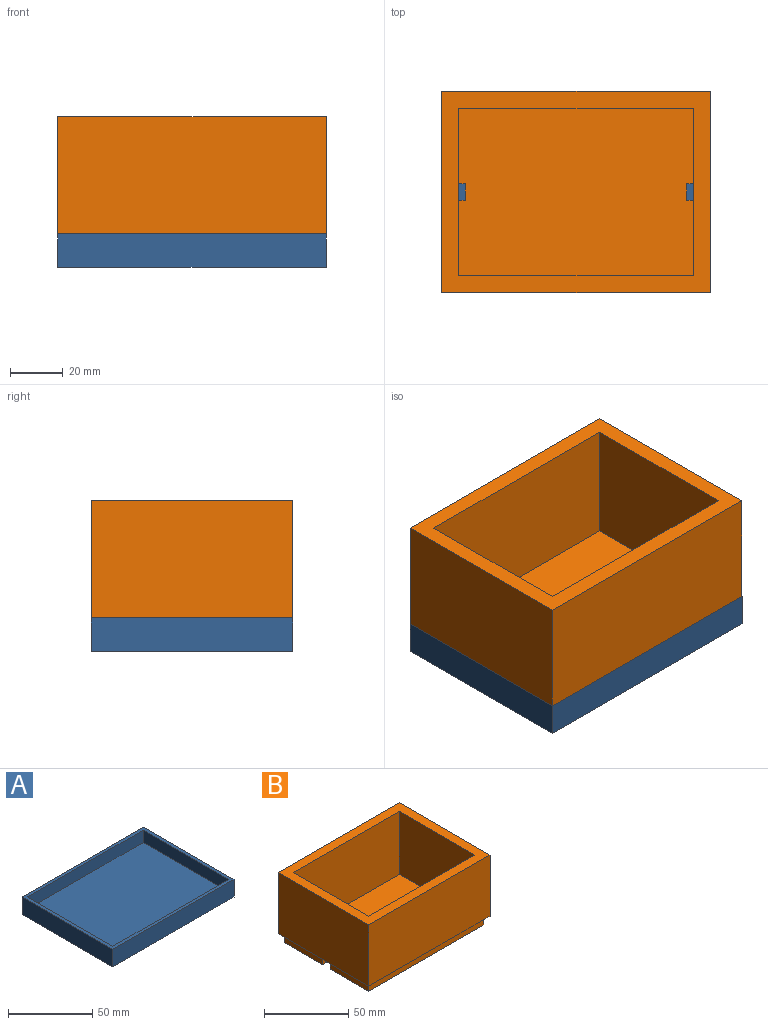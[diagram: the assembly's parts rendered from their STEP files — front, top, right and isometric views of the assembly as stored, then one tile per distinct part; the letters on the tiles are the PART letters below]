
ASSEMBLY  parts=2 mates=1
PART A: 11 faces, bbox 101.6x76.2x12.7 mm
  f0: plane 101.6x76.2mm, normal (0,0,1), area 792mm2, adj f1,f2,f3,f4,f6,f7,f8,f9
  f1: plane 101.6x12.7mm, normal (0,1,0), area 1290.3mm2, adj f0,f2,f4,f5
  f2: plane 76.2x12.7mm, normal (-1,0,0), area 967.7mm2, adj f0,f1,f3,f5
  f3: plane 101.6x12.7mm, normal (0,-1,0), area 1290.3mm2, adj f0,f2,f4,f5
  f4: plane 76.2x12.7mm, normal (1,0,0), area 967.7mm2, adj f0,f1,f3,f5
  f5: plane 101.6x76.2mm, normal (0,0,-1), area 7741.9mm2, adj f1,f2,f3,f4
  f6: plane 97.03x8.89mm, normal (0,-1,0), area 862.6mm2, adj f0,f7,f9,f10
  f7: plane 71.63x8.89mm, normal (1,0,0), area 636.8mm2, adj f0,f6,f8,f10
  f8: plane 97.03x8.89mm, normal (0,1,0), area 862.6mm2, adj f0,f7,f9,f10
  f9: plane 71.63x8.89mm, normal (-1,0,0), area 636.8mm2, adj f0,f6,f8,f10
  f10: plane 97.03x71.63mm, normal (0,0,1), area 6949.9mm2, adj f6,f7,f8,f9
PART B: 24 faces, bbox 101.6x76.2x50.8 mm
  f0: plane 32.39x6.35mm, normal (-1,0,0), area 205.6mm2, adj f14,f16,f17,f21
  f1: plane 88.9x63.5mm, normal (0,0,1), area 5612.9mm2, adj f2,f4,f10,f11,f18,f19,f20,f21
  f2: plane 63.5x45.72mm, normal (1,0,0), area 2895.2mm2, adj f1,f5,f10,f11,f16,f21,f22
  f3: plane 32.39x6.35mm, normal (1,0,0), area 205.6mm2, adj f12,f16,f17,f18
  f4: plane 63.5x45.72mm, normal (-1,0,0), area 2895.2mm2, adj f1,f5,f10,f11,f16,f18,f19
  f5: plane 101.6x76.2mm, normal (0,0,1), area 2096.8mm2, adj f2,f4,f6,f7,f8,f9,f10,f11
  f6: plane 101.6x44.45mm, normal (0,1,0), area 4516.1mm2, adj f5,f7,f9,f16
  f7: plane 76.2x44.45mm, normal (-1,0,0), area 3387.1mm2, adj f5,f6,f8,f16
  f8: plane 101.6x44.45mm, normal (0,-1,0), area 4516.1mm2, adj f5,f7,f9,f16
  f9: plane 76.2x44.45mm, normal (1,0,0), area 3387.1mm2, adj f5,f6,f8,f16
  f10: plane 88.9x45.72mm, normal (0,1,0), area 4064.5mm2, adj f1,f2,f4,f5
  f11: plane 88.9x45.72mm, normal (0,-1,0), area 4064.5mm2, adj f1,f2,f4,f5
  f12: plane 96.52x6.35mm, normal (0,-1,0), area 612.9mm2, adj f3,f15,f16,f17
  f13: plane 32.39x6.35mm, normal (1,0,0), area 205.6mm2, adj f14,f16,f17,f19
  f14: plane 96.52x6.35mm, normal (0,1,0), area 612.9mm2, adj f0,f13,f16,f17
  f15: plane 32.39x6.35mm, normal (-1,0,0), area 205.6mm2, adj f12,f16,f17,f22
  f16: plane 101.6x76.2mm, normal (0,0,-1), area 925.8mm2, adj f0,f2,f3,f4,f6,f7,f8,f9
  f17: plane 96.52x71.12mm, normal (0,0,-1), area 6783.9mm2, adj f0,f3,f12,f13,f14,f15,f18,f19
  f18: plane 6.35x6.35mm, normal (0,1,0), area 37.1mm2, adj f1,f3,f4,f16,f17,f20
  f19: plane 6.35x6.35mm, normal (0,-1,0), area 37.1mm2, adj f1,f4,f13,f16,f17,f20
  f20: plane 6.35x5.08mm, normal (1,0,0), area 32.3mm2, adj f1,f17,f18,f19
  f21: plane 6.35x6.35mm, normal (0,-1,0), area 37.1mm2, adj f0,f1,f2,f16,f17,f23
  f22: plane 6.35x6.35mm, normal (0,1,0), area 37.1mm2, adj f1,f2,f15,f16,f17,f23
  f23: plane 6.35x5.08mm, normal (-1,0,0), area 32.3mm2, adj f1,f17,f21,f22
PLACE A t=(7.22,0.85,-42.6)mm
PLACE B t=(-10.83,12.76,-36.25)mm
MATE fastened B.f8 <-> A.f3  axis (0,-1,0) through (-3.61,-28.78,-29.9)mm
